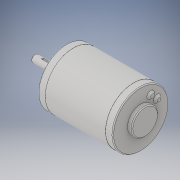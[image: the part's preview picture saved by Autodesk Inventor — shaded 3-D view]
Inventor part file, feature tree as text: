
AUTODESK INVENTOR PART (.ipt)
format: ipt  version: 2018 (Build 220112000, 112)  size: 169,472 bytes
history: native  units: in
note: dims shown in document units (in); Inventor stores cm internally (conversion verified against a paired STEP export)
features: chamfer x1
ambient origin geometry x8: Origin, YZ Plane, XZ Plane, XY Plane, X Axis, Y Axis, Z Axis, Center Point
bodies: Solid1 (feature_tree)
feature tree (1):
  chamfer  "Chamfer3"  [1 undecoded]
note: 1 required parameter value undecoded (feature->parameter linkage not recoverable at this tier; creation-order binding heuristic only, values carry confidence <= 0.55)
